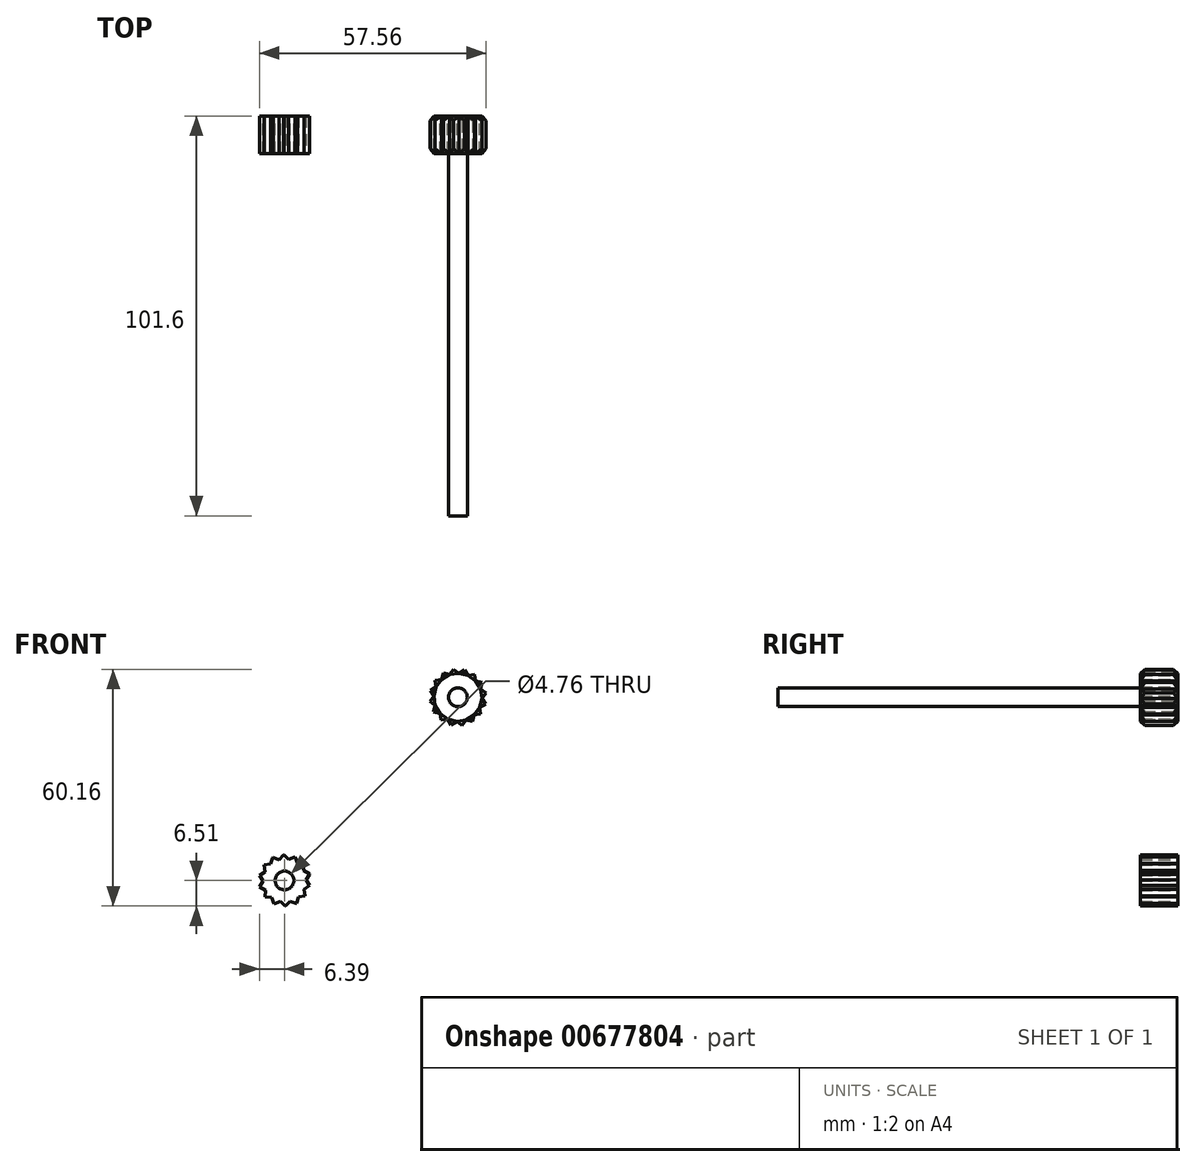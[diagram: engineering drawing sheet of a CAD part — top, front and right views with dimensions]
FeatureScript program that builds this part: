
annotation { "Feature Type Name" : "Feature", "Feature Type Description" : "" }
export const myFeature = defineFeature(function(context is Context, id is Id, definition is map)
    precondition{}
    {
        {
            var Q0;
            Q0=qCreatedBy(makeId("Front.planeOp"),FACE);
            var sketch = newSketch(context, id + "F0", { "sketchPlane" : qUnion([Q0])});
            skCircle(sketch, "E0.cCircle", {"center": v(0, 0) * mm, "radius": 5.32 * mm, "construction": true});
            skLineSegment(sketch, "E0.0", {"start": v(4.98, -2.23) * mm, "end": v(3.52, -4.17) * mm});
            skLineSegment(sketch, "E0.1", {"start": v(3.52, -4.17) * mm, "end": v(1.36, -5.29) * mm});
            skLineSegment(sketch, "E0.2", {"start": v(1.36, -5.29) * mm, "end": v(-1.07, -5.35) * mm});
            skLineSegment(sketch, "E0.3", {"start": v(-1.07, -5.35) * mm, "end": v(-3.28, -4.36) * mm});
            skLineSegment(sketch, "E0.4", {"start": v(-3.28, -4.36) * mm, "end": v(-4.85, -2.5) * mm});
            skLineSegment(sketch, "E0.5", {"start": v(-4.85, -2.5) * mm, "end": v(-5.46, -0.15) * mm});
            skLineSegment(sketch, "E0.6", {"start": v(-5.46, -0.15) * mm, "end": v(-4.98, 2.23) * mm});
            skLineSegment(sketch, "E0.7", {"start": v(-4.98, 2.23) * mm, "end": v(-3.52, 4.17) * mm});
            skLineSegment(sketch, "E0.8", {"start": v(-3.52, 4.17) * mm, "end": v(-1.36, 5.29) * mm});
            skLineSegment(sketch, "E0.9", {"start": v(-1.36, 5.29) * mm, "end": v(1.07, 5.35) * mm});
            skLineSegment(sketch, "E0.10", {"start": v(1.07, 5.35) * mm, "end": v(3.28, 4.36) * mm});
            skLineSegment(sketch, "E0.11", {"start": v(3.28, 4.36) * mm, "end": v(4.85, 2.5) * mm});
            skLineSegment(sketch, "E0.12", {"start": v(4.85, 2.5) * mm, "end": v(5.46, 0.15) * mm});
            skLineSegment(sketch, "E0.13", {"start": v(5.46, 0.15) * mm, "end": v(4.98, -2.23) * mm});
            skPoint(sketch, "E0.0.midPoint", {"position": v(4.25, -3.2) * mm});
            skSolve(sketch);
        }
        {
            var Q0;
            Q0 = qSketchRegion(id + "F0", true);
            extrude(context, id + "F1", {"entities" : qUnion([Q0]), "depth" : 9.52 * mm, "offsetDistance" : 25.4 * mm});
        }
        {
            var Q0;
            Q0=makeQuery(id+"F1.opExtrude","SWEPT_FACE",FACE,{"disambiguationData":[OSD([sQuery(id+"F0.wireOp",EDGE,"E0.12")])]});
            extrude(context, id + "F2", {"entities" : qUnion([Q0]), "operationType" : NewBodyOperationType.ADD, "depth" : 1.2 * mm, "offsetDistance" : 25.4 * mm});
        }
        {
            var Q0;
            Q0=makeQuery(id+"F1.opExtrude","SWEPT_FACE",FACE,{"disambiguationData":[OSD([sQuery(id+"F0.wireOp",EDGE,"E0.13")])]});
            extrude(context, id + "F3", {"entities" : qUnion([Q0]), "operationType" : NewBodyOperationType.ADD, "depth" : 1.2 * mm, "offsetDistance" : 25.4 * mm});
        }
        {
            var Q0;
            Q0=makeQuery(id+"F1.opExtrude","SWEPT_FACE",FACE,{"disambiguationData":[OSD([sQuery(id+"F0.wireOp",EDGE,"E0.0")])]});
            extrude(context, id + "F4", {"entities" : qUnion([Q0]), "operationType" : NewBodyOperationType.ADD, "depth" : 1.2 * mm, "offsetDistance" : 25.4 * mm});
        }
        {
            var Q0;
            Q0=makeQuery(id+"F1.opExtrude","SWEPT_FACE",FACE,{"disambiguationData":[OSD([sQuery(id+"F0.wireOp",EDGE,"E0.11")])]});
            extrude(context, id + "F5", {"entities" : qUnion([Q0]), "operationType" : NewBodyOperationType.ADD, "depth" : 1.2 * mm, "offsetDistance" : 25.4 * mm});
        }
        {
            var Q0;
            Q0=makeQuery(id+"F1.opExtrude","SWEPT_FACE",FACE,{"disambiguationData":[OSD([sQuery(id+"F0.wireOp",EDGE,"E0.10")])]});
            extrude(context, id + "F6", {"entities" : qUnion([Q0]), "operationType" : NewBodyOperationType.ADD, "depth" : 1.2 * mm, "offsetDistance" : 25.4 * mm});
        }
        {
            var Q0;
            Q0=makeQuery(id+"F1.opExtrude","SWEPT_FACE",FACE,{"disambiguationData":[OSD([sQuery(id+"F0.wireOp",EDGE,"E0.9")])]});
            extrude(context, id + "F7", {"entities" : qUnion([Q0]), "operationType" : NewBodyOperationType.ADD, "depth" : 1.2 * mm, "offsetDistance" : 25.4 * mm});
        }
        {
            var Q0;
            Q0=makeQuery(id+"F1.opExtrude","SWEPT_FACE",FACE,{"disambiguationData":[OSD([sQuery(id+"F0.wireOp",EDGE,"E0.8")])]});
            extrude(context, id + "F8", {"entities" : qUnion([Q0]), "operationType" : NewBodyOperationType.ADD, "depth" : 1.2 * mm, "offsetDistance" : 25.4 * mm});
        }
        {
            var Q0;
            Q0=makeQuery(id+"F1.opExtrude","SWEPT_FACE",FACE,{"disambiguationData":[OSD([sQuery(id+"F0.wireOp",EDGE,"E0.7")])]});
            extrude(context, id + "F9", {"entities" : qUnion([Q0]), "operationType" : NewBodyOperationType.ADD, "depth" : 1.2 * mm, "offsetDistance" : 25.4 * mm});
        }
        {
            var Q0;
            Q0=makeQuery(id+"F1.opExtrude","SWEPT_FACE",FACE,{"disambiguationData":[OSD([sQuery(id+"F0.wireOp",EDGE,"E0.6")])]});
            extrude(context, id + "F10", {"entities" : qUnion([Q0]), "operationType" : NewBodyOperationType.ADD, "depth" : 1.2 * mm, "offsetDistance" : 25.4 * mm});
        }
        {
            var Q0;
            Q0=makeQuery(id+"F1.opExtrude","SWEPT_FACE",FACE,{"disambiguationData":[OSD([sQuery(id+"F0.wireOp",EDGE,"E0.5")])]});
            extrude(context, id + "F11", {"entities" : qUnion([Q0]), "operationType" : NewBodyOperationType.ADD, "depth" : 1.2 * mm, "offsetDistance" : 25.4 * mm});
        }
        {
            var Q0;
            Q0=makeQuery(id+"F1.opExtrude","SWEPT_FACE",FACE,{"disambiguationData":[OSD([sQuery(id+"F0.wireOp",EDGE,"E0.4")])]});
            extrude(context, id + "F12", {"entities" : qUnion([Q0]), "operationType" : NewBodyOperationType.ADD, "depth" : 1.2 * mm, "offsetDistance" : 25.4 * mm});
        }
        {
            var Q0;
            Q0=makeQuery(id+"F1.opExtrude","SWEPT_FACE",FACE,{"disambiguationData":[OSD([sQuery(id+"F0.wireOp",EDGE,"E0.3")])]});
            extrude(context, id + "F13", {"entities" : qUnion([Q0]), "operationType" : NewBodyOperationType.ADD, "depth" : 1.2 * mm, "offsetDistance" : 25.4 * mm});
        }
        {
            var Q0;
            Q0=makeQuery(id+"F1.opExtrude","SWEPT_FACE",FACE,{"disambiguationData":[OSD([sQuery(id+"F0.wireOp",EDGE,"E0.2")])]});
            extrude(context, id + "F14", {"entities" : qUnion([Q0]), "operationType" : NewBodyOperationType.ADD, "depth" : 1.2 * mm, "offsetDistance" : 25.4 * mm});
        }
        {
            var Q0;
            Q0=makeQuery(id+"F1.opExtrude","SWEPT_FACE",FACE,{"disambiguationData":[OSD([sQuery(id+"F0.wireOp",EDGE,"E0.1")])]});
            extrude(context, id + "F15", {"entities" : qUnion([Q0]), "operationType" : NewBodyOperationType.ADD, "depth" : 1.2 * mm, "offsetDistance" : 25.4 * mm});
        }
        {
            var Q0;
            Q0=makeQuery(id+"F4.opExtrude","CAP_EDGE",EDGE,{"disambiguationData":[OSD([sQuery(id+"F0.wireOp",EDGE,"E0.0"),sQuery(id+"F0.wireOp",EDGE,"E0.1")])],"isStart":false});
            var Q1;
            Q1=makeQuery(id+"F15.opExtrude","CAP_EDGE",EDGE,{"disambiguationData":[OSD([sQuery(id+"F0.wireOp",EDGE,"E0.0"),sQuery(id+"F0.wireOp",EDGE,"E0.1")])],"isStart":false});
            var Q2;
            Q2=makeQuery(id+"F15.opExtrude","CAP_EDGE",EDGE,{"disambiguationData":[OSD([sQuery(id+"F0.wireOp",EDGE,"E0.1"),sQuery(id+"F0.wireOp",EDGE,"E0.2")])],"isStart":false});
            var Q3;
            Q3=makeQuery(id+"F4.opExtrude","CAP_EDGE",EDGE,{"disambiguationData":[OSD([sQuery(id+"F0.wireOp",EDGE,"E0.0"),sQuery(id+"F0.wireOp",EDGE,"E0.13")])],"isStart":false});
            var Q4;
            Q4=makeQuery(id+"F3.opExtrude","CAP_EDGE",EDGE,{"disambiguationData":[OSD([sQuery(id+"F0.wireOp",EDGE,"E0.0"),sQuery(id+"F0.wireOp",EDGE,"E0.13")])],"isStart":false});
            var Q5;
            Q5=makeQuery(id+"F3.opExtrude","CAP_EDGE",EDGE,{"disambiguationData":[OSD([sQuery(id+"F0.wireOp",EDGE,"E0.12"),sQuery(id+"F0.wireOp",EDGE,"E0.13")])],"isStart":false});
            var Q6;
            Q6=makeQuery(id+"F2.opExtrude","CAP_EDGE",EDGE,{"disambiguationData":[OSD([sQuery(id+"F0.wireOp",EDGE,"E0.12"),sQuery(id+"F0.wireOp",EDGE,"E0.13")])],"isStart":false});
            var Q7;
            Q7=makeQuery(id+"F5.opExtrude","CAP_EDGE",EDGE,{"disambiguationData":[OSD([sQuery(id+"F0.wireOp",EDGE,"E0.11"),sQuery(id+"F0.wireOp",EDGE,"E0.12")])],"isStart":false});
            var Q8;
            Q8=makeQuery(id+"F2.opExtrude","CAP_EDGE",EDGE,{"disambiguationData":[OSD([sQuery(id+"F0.wireOp",EDGE,"E0.11"),sQuery(id+"F0.wireOp",EDGE,"E0.12")])],"isStart":false});
            var Q9;
            Q9=makeQuery(id+"F5.opExtrude","CAP_EDGE",EDGE,{"disambiguationData":[OSD([sQuery(id+"F0.wireOp",EDGE,"E0.10"),sQuery(id+"F0.wireOp",EDGE,"E0.11")])],"isStart":false});
            var Q10;
            Q10=makeQuery(id+"F6.opExtrude","CAP_EDGE",EDGE,{"disambiguationData":[OSD([sQuery(id+"F0.wireOp",EDGE,"E0.10"),sQuery(id+"F0.wireOp",EDGE,"E0.11")])],"isStart":false});
            var Q11;
            Q11=makeQuery(id+"F6.opExtrude","CAP_EDGE",EDGE,{"disambiguationData":[OSD([sQuery(id+"F0.wireOp",EDGE,"E0.9"),sQuery(id+"F0.wireOp",EDGE,"E0.10")])],"isStart":false});
            var Q12;
            Q12=makeQuery(id+"F7.opExtrude","CAP_EDGE",EDGE,{"disambiguationData":[OSD([sQuery(id+"F0.wireOp",EDGE,"E0.9"),sQuery(id+"F0.wireOp",EDGE,"E0.10")])],"isStart":false});
            var Q13;
            Q13=makeQuery(id+"F8.opExtrude","CAP_EDGE",EDGE,{"disambiguationData":[OSD([sQuery(id+"F0.wireOp",EDGE,"E0.8"),sQuery(id+"F0.wireOp",EDGE,"E0.9")])],"isStart":false});
            var Q14;
            Q14=makeQuery(id+"F7.opExtrude","CAP_EDGE",EDGE,{"disambiguationData":[OSD([sQuery(id+"F0.wireOp",EDGE,"E0.8"),sQuery(id+"F0.wireOp",EDGE,"E0.9")])],"isStart":false});
            var Q15;
            Q15=makeQuery(id+"F8.opExtrude","CAP_EDGE",EDGE,{"disambiguationData":[OSD([sQuery(id+"F0.wireOp",EDGE,"E0.7"),sQuery(id+"F0.wireOp",EDGE,"E0.8")])],"isStart":false});
            var Q16;
            Q16=makeQuery(id+"F9.opExtrude","CAP_EDGE",EDGE,{"disambiguationData":[OSD([sQuery(id+"F0.wireOp",EDGE,"E0.7"),sQuery(id+"F0.wireOp",EDGE,"E0.8")])],"isStart":false});
            var Q17;
            Q17=makeQuery(id+"F10.opExtrude","CAP_EDGE",EDGE,{"disambiguationData":[OSD([sQuery(id+"F0.wireOp",EDGE,"E0.6"),sQuery(id+"F0.wireOp",EDGE,"E0.7")])],"isStart":false});
            var Q18;
            Q18=makeQuery(id+"F9.opExtrude","CAP_EDGE",EDGE,{"disambiguationData":[OSD([sQuery(id+"F0.wireOp",EDGE,"E0.6"),sQuery(id+"F0.wireOp",EDGE,"E0.7")])],"isStart":false});
            var Q19;
            Q19=makeQuery(id+"F10.opExtrude","CAP_EDGE",EDGE,{"disambiguationData":[OSD([sQuery(id+"F0.wireOp",EDGE,"E0.5"),sQuery(id+"F0.wireOp",EDGE,"E0.6")])],"isStart":false});
            var Q20;
            Q20=makeQuery(id+"F11.opExtrude","CAP_EDGE",EDGE,{"disambiguationData":[OSD([sQuery(id+"F0.wireOp",EDGE,"E0.5"),sQuery(id+"F0.wireOp",EDGE,"E0.6")])],"isStart":false});
            var Q21;
            Q21=makeQuery(id+"F11.opExtrude","CAP_EDGE",EDGE,{"disambiguationData":[OSD([sQuery(id+"F0.wireOp",EDGE,"E0.4"),sQuery(id+"F0.wireOp",EDGE,"E0.5")])],"isStart":false});
            var Q22;
            Q22=makeQuery(id+"F12.opExtrude","CAP_EDGE",EDGE,{"disambiguationData":[OSD([sQuery(id+"F0.wireOp",EDGE,"E0.4"),sQuery(id+"F0.wireOp",EDGE,"E0.5")])],"isStart":false});
            var Q23;
            Q23=makeQuery(id+"F13.opExtrude","CAP_EDGE",EDGE,{"disambiguationData":[OSD([sQuery(id+"F0.wireOp",EDGE,"E0.3"),sQuery(id+"F0.wireOp",EDGE,"E0.4")])],"isStart":false});
            var Q24;
            Q24=makeQuery(id+"F12.opExtrude","CAP_EDGE",EDGE,{"disambiguationData":[OSD([sQuery(id+"F0.wireOp",EDGE,"E0.3"),sQuery(id+"F0.wireOp",EDGE,"E0.4")])],"isStart":false});
            var Q25;
            Q25=makeQuery(id+"F13.opExtrude","CAP_EDGE",EDGE,{"disambiguationData":[OSD([sQuery(id+"F0.wireOp",EDGE,"E0.2"),sQuery(id+"F0.wireOp",EDGE,"E0.3")])],"isStart":false});
            var Q26;
            Q26=makeQuery(id+"F14.opExtrude","CAP_EDGE",EDGE,{"disambiguationData":[OSD([sQuery(id+"F0.wireOp",EDGE,"E0.2"),sQuery(id+"F0.wireOp",EDGE,"E0.3")])],"isStart":false});
            var Q27;
            Q27=makeQuery(id+"F14.opExtrude","CAP_EDGE",EDGE,{"disambiguationData":[OSD([sQuery(id+"F0.wireOp",EDGE,"E0.1"),sQuery(id+"F0.wireOp",EDGE,"E0.2")])],"isStart":false});
            chamfer(context, id + "F16", {"entities" : qUnion([Q0, Q1, Q2, Q3, Q4, Q5, Q6, Q7, Q8, Q9, Q10, Q11, Q12, Q13, Q14, Q15, Q16, Q17, Q18, Q19, Q20, Q21, Q22, Q23, Q24, Q25, Q26, Q27]), "width" : 1.2 * mm, "tangentPropagation" : true});
        }
        {
            var Q0;
            Q0=sQuery(id+"F0.wireOp",VERTEX,"E0.cCircle.center");
            var Q1;
            Q1=makeQuery(id+"F1.opExtrude","SWEPT_BODY",BODY,{"disambiguationData":[OSD([sQuery(id+"F0.wireOp",EDGE,"E0.0"),sQuery(id+"F0.wireOp",EDGE,"E0.1"),sQuery(id+"F0.wireOp",EDGE,"E0.2"),sQuery(id+"F0.wireOp",EDGE,"E0.3"),sQuery(id+"F0.wireOp",EDGE,"E0.4"),sQuery(id+"F0.wireOp",EDGE,"E0.5"),sQuery(id+"F0.wireOp",EDGE,"E0.6"),sQuery(id+"F0.wireOp",EDGE,"E0.7"),sQuery(id+"F0.wireOp",EDGE,"E0.8"),sQuery(id+"F0.wireOp",EDGE,"E0.9"),sQuery(id+"F0.wireOp",EDGE,"E0.10"),sQuery(id+"F0.wireOp",EDGE,"E0.11"),sQuery(id+"F0.wireOp",EDGE,"E0.12"),sQuery(id+"F0.wireOp",EDGE,"E0.13")])]});
            hole(context, id + "F17", {"style" : HoleStyle.SIMPLE, "endStyle" : HoleEndStyle.THROUGH, "oppositeDirection" : true, "holeDiameter" : 4.76 * mm, "majorDiameter" : 6.35 * mm, "isTappedThrough" : true, "tappedDepth" : 12.7 * mm, "tapClearance" : 3, "locations" : qUnion([Q0]), "scope" : qUnion([Q1])});
        }
        {
            var Q0;
            Q0=qCreatedBy(makeId("Front.planeOp"),FACE);
            var sketch = newSketch(context, id + "F18", { "sketchPlane" : qUnion([Q0])});
            skCircle(sketch, "E1.cCircle", {"center": v(44.05, 46.54) * mm, "radius": 6 * mm, "construction": true});
            skLineSegment(sketch, "E1.0", {"start": v(50.16, 46.25) * mm, "end": v(49.59, 43.93) * mm});
            skLineSegment(sketch, "E1.1", {"start": v(49.59, 43.93) * mm, "end": v(48.17, 42) * mm});
            skLineSegment(sketch, "E1.2", {"start": v(48.17, 42) * mm, "end": v(46.12, 40.78) * mm});
            skLineSegment(sketch, "E1.3", {"start": v(46.12, 40.78) * mm, "end": v(43.76, 40.42) * mm});
            skLineSegment(sketch, "E1.4", {"start": v(43.76, 40.42) * mm, "end": v(41.45, 41) * mm});
            skLineSegment(sketch, "E1.5", {"start": v(41.45, 41) * mm, "end": v(39.52, 42.42) * mm});
            skLineSegment(sketch, "E1.6", {"start": v(39.52, 42.42) * mm, "end": v(38.3, 44.46) * mm});
            skLineSegment(sketch, "E1.7", {"start": v(38.3, 44.46) * mm, "end": v(37.94, 46.82) * mm});
            skLineSegment(sketch, "E1.8", {"start": v(37.94, 46.82) * mm, "end": v(38.51, 49.14) * mm});
            skLineSegment(sketch, "E1.9", {"start": v(38.51, 49.14) * mm, "end": v(39.93, 51.06) * mm});
            skLineSegment(sketch, "E1.10", {"start": v(39.93, 51.06) * mm, "end": v(41.98, 52.3) * mm});
            skLineSegment(sketch, "E1.11", {"start": v(41.98, 52.3) * mm, "end": v(44.34, 52.65) * mm});
            skLineSegment(sketch, "E1.12", {"start": v(44.34, 52.65) * mm, "end": v(46.66, 52.07) * mm});
            skLineSegment(sketch, "E1.13", {"start": v(46.66, 52.07) * mm, "end": v(48.58, 50.65) * mm});
            skLineSegment(sketch, "E1.14", {"start": v(48.58, 50.65) * mm, "end": v(49.8, 48.6) * mm});
            skLineSegment(sketch, "E1.15", {"start": v(49.8, 48.6) * mm, "end": v(50.16, 46.25) * mm});
            skPoint(sketch, "E1.0.midPoint", {"position": v(49.88, 45.09) * mm});
            skCircle(sketch, "E2", {"center": v(44.05, 46.54) * mm, "radius": 2.38 * mm});
            skSolve(sketch);
        }
        {
            var Q0;
            Q0=makeQuery(id+"F18.imprint","IMPRINT",FACE,{"disambiguationData":[TD([[makeQuery(id+"F18.imprint","IMPRINT",EDGE,{"derivedFrom":sQuery(id+"F18.wireOp",EDGE,"E1.0")}),-1.0]])]});
            extrude(context, id + "F19", {"entities" : qUnion([Q0]), "depth" : 9.52 * mm, "offsetDistance" : 25.4 * mm});
        }
        {
            var Q0;
            Q0=makeQuery(id+"F19.opExtrude","SWEPT_FACE",FACE,{"disambiguationData":[OSD([sQuery(id+"F18.wireOp",EDGE,"E1.2")])]});
            extrude(context, id + "F20", {"entities" : qUnion([Q0]), "operationType" : NewBodyOperationType.ADD, "depth" : 1.2 * mm, "offsetDistance" : 25.4 * mm});
        }
        {
            var Q0;
            Q0=makeQuery(id+"F19.opExtrude","SWEPT_FACE",FACE,{"disambiguationData":[OSD([sQuery(id+"F18.wireOp",EDGE,"E1.4")])]});
            extrude(context, id + "F21", {"entities" : qUnion([Q0]), "operationType" : NewBodyOperationType.ADD, "depth" : 1.2 * mm, "offsetDistance" : 25.4 * mm});
        }
        {
            var Q0;
            Q0=makeQuery(id+"F19.opExtrude","SWEPT_FACE",FACE,{"disambiguationData":[OSD([sQuery(id+"F18.wireOp",EDGE,"E1.6")])]});
            extrude(context, id + "F22", {"entities" : qUnion([Q0]), "operationType" : NewBodyOperationType.ADD, "depth" : 1.2 * mm, "offsetDistance" : 25.4 * mm});
        }
        {
            var Q0;
            Q0=makeQuery(id+"F19.opExtrude","SWEPT_FACE",FACE,{"disambiguationData":[OSD([sQuery(id+"F18.wireOp",EDGE,"E1.8")])]});
            extrude(context, id + "F23", {"entities" : qUnion([Q0]), "operationType" : NewBodyOperationType.ADD, "depth" : 1.2 * mm, "offsetDistance" : 25.4 * mm});
        }
        {
            var Q0;
            Q0=makeQuery(id+"F19.opExtrude","SWEPT_FACE",FACE,{"disambiguationData":[OSD([sQuery(id+"F18.wireOp",EDGE,"E1.10")])]});
            extrude(context, id + "F24", {"entities" : qUnion([Q0]), "operationType" : NewBodyOperationType.ADD, "depth" : 1.2 * mm, "offsetDistance" : 25.4 * mm});
        }
        {
            var Q0;
            Q0=makeQuery(id+"F19.opExtrude","SWEPT_FACE",FACE,{"disambiguationData":[OSD([sQuery(id+"F18.wireOp",EDGE,"E1.12")])]});
            extrude(context, id + "F25", {"entities" : qUnion([Q0]), "operationType" : NewBodyOperationType.ADD, "depth" : 1.2 * mm, "offsetDistance" : 25.4 * mm});
        }
        {
            var Q0;
            Q0=makeQuery(id+"F19.opExtrude","SWEPT_FACE",FACE,{"disambiguationData":[OSD([sQuery(id+"F18.wireOp",EDGE,"E1.14")])]});
            extrude(context, id + "F26", {"entities" : qUnion([Q0]), "operationType" : NewBodyOperationType.ADD, "depth" : 1.2 * mm, "offsetDistance" : 25.4 * mm});
        }
        {
            var Q0;
            Q0=makeQuery(id+"F19.opExtrude","SWEPT_FACE",FACE,{"disambiguationData":[OSD([sQuery(id+"F18.wireOp",EDGE,"E1.0")])]});
            extrude(context, id + "F27", {"entities" : qUnion([Q0]), "operationType" : NewBodyOperationType.ADD, "depth" : 1.2 * mm, "offsetDistance" : 25.4 * mm});
        }
        {
            var Q0;
            Q0=makeQuery(id+"F26.opExtrude","CAP_FACE",FACE,{"disambiguationData":[OSD([sQuery(id+"F18.wireOp",EDGE,"E1.14")])],"isStart":false});
            var Q1;
            Q1=makeQuery(id+"F25.opExtrude","CAP_FACE",FACE,{"disambiguationData":[OSD([sQuery(id+"F18.wireOp",EDGE,"E1.12")])],"isStart":false});
            var Q2;
            Q2=makeQuery(id+"F27.opExtrude","CAP_FACE",FACE,{"disambiguationData":[OSD([sQuery(id+"F18.wireOp",EDGE,"E1.0")])],"isStart":false});
            var Q3;
            Q3=makeQuery(id+"F20.opExtrude","CAP_FACE",FACE,{"disambiguationData":[OSD([sQuery(id+"F18.wireOp",EDGE,"E1.2")])],"isStart":false});
            var Q4;
            Q4=makeQuery(id+"F21.opExtrude","CAP_FACE",FACE,{"disambiguationData":[OSD([sQuery(id+"F18.wireOp",EDGE,"E1.4")])],"isStart":false});
            var Q5;
            Q5=makeQuery(id+"F22.opExtrude","CAP_FACE",FACE,{"disambiguationData":[OSD([sQuery(id+"F18.wireOp",EDGE,"E1.6")])],"isStart":false});
            var Q6;
            Q6=makeQuery(id+"F23.opExtrude","CAP_FACE",FACE,{"disambiguationData":[OSD([sQuery(id+"F18.wireOp",EDGE,"E1.8")])],"isStart":false});
            var Q7;
            Q7=makeQuery(id+"F24.opExtrude","CAP_FACE",FACE,{"disambiguationData":[OSD([sQuery(id+"F18.wireOp",EDGE,"E1.10")])],"isStart":false});
            chamfer(context, id + "F28", {"entities" : qUnion([Q0, Q1, Q2, Q3, Q4, Q5, Q6, Q7]), "width" : 1.2 * mm, "tangentPropagation" : true});
        }
        {
            var Q0;
            Q0=makeQuery(id+"F19.opExtrude","SWEPT_FACE",FACE,{"disambiguationData":[OSD([sQuery(id+"F18.wireOp",EDGE,"E1.9")])]});
            extrude(context, id + "F29", {"entities" : qUnion([Q0]), "operationType" : NewBodyOperationType.ADD, "depth" : 1.2 * mm, "offsetDistance" : 25.4 * mm});
        }
        {
            var Q0;
            Q0=makeQuery(id+"F19.opExtrude","SWEPT_FACE",FACE,{"disambiguationData":[OSD([sQuery(id+"F18.wireOp",EDGE,"E1.11")])]});
            extrude(context, id + "F30", {"entities" : qUnion([Q0]), "operationType" : NewBodyOperationType.ADD, "depth" : 1.2 * mm, "offsetDistance" : 25.4 * mm});
        }
        {
            var Q0;
            Q0=makeQuery(id+"F19.opExtrude","SWEPT_FACE",FACE,{"disambiguationData":[OSD([sQuery(id+"F18.wireOp",EDGE,"E1.13")])]});
            extrude(context, id + "F31", {"entities" : qUnion([Q0]), "operationType" : NewBodyOperationType.ADD, "depth" : 1.2 * mm, "offsetDistance" : 25.4 * mm});
        }
        {
            var Q0;
            Q0=makeQuery(id+"F19.opExtrude","SWEPT_FACE",FACE,{"disambiguationData":[OSD([sQuery(id+"F18.wireOp",EDGE,"E1.15")])]});
            extrude(context, id + "F32", {"entities" : qUnion([Q0]), "operationType" : NewBodyOperationType.ADD, "depth" : 1.2 * mm, "offsetDistance" : 25.4 * mm});
        }
        {
            var Q0;
            Q0=makeQuery(id+"F19.opExtrude","SWEPT_FACE",FACE,{"disambiguationData":[OSD([sQuery(id+"F18.wireOp",EDGE,"E1.1")])]});
            extrude(context, id + "F33", {"entities" : qUnion([Q0]), "operationType" : NewBodyOperationType.ADD, "depth" : 1.2 * mm, "offsetDistance" : 25.4 * mm});
        }
        {
            var Q0;
            Q0=makeQuery(id+"F19.opExtrude","SWEPT_FACE",FACE,{"disambiguationData":[OSD([sQuery(id+"F18.wireOp",EDGE,"E1.3")])]});
            extrude(context, id + "F34", {"entities" : qUnion([Q0]), "operationType" : NewBodyOperationType.ADD, "depth" : 1.2 * mm, "offsetDistance" : 25.4 * mm});
        }
        {
            var Q0;
            Q0=makeQuery(id+"F19.opExtrude","SWEPT_FACE",FACE,{"disambiguationData":[OSD([sQuery(id+"F18.wireOp",EDGE,"E1.5")])]});
            extrude(context, id + "F35", {"entities" : qUnion([Q0]), "operationType" : NewBodyOperationType.ADD, "depth" : 1.2 * mm, "offsetDistance" : 25.4 * mm});
        }
        {
            var Q0;
            Q0=makeQuery(id+"F19.opExtrude","SWEPT_FACE",FACE,{"disambiguationData":[OSD([sQuery(id+"F18.wireOp",EDGE,"E1.7")])]});
            extrude(context, id + "F36", {"entities" : qUnion([Q0]), "operationType" : NewBodyOperationType.ADD, "depth" : 1.2 * mm, "offsetDistance" : 25.4 * mm});
        }
        {
            var Q0;
            Q0=makeQuery(id+"F36.opExtrude","CAP_FACE",FACE,{"disambiguationData":[OSD([sQuery(id+"F18.wireOp",EDGE,"E1.7")])],"isStart":false});
            var Q1;
            Q1=makeQuery(id+"F29.opExtrude","CAP_FACE",FACE,{"disambiguationData":[OSD([sQuery(id+"F18.wireOp",EDGE,"E1.9")])],"isStart":false});
            var Q2;
            Q2=makeQuery(id+"F35.opExtrude","CAP_FACE",FACE,{"disambiguationData":[OSD([sQuery(id+"F18.wireOp",EDGE,"E1.5")])],"isStart":false});
            var Q3;
            Q3=makeQuery(id+"F34.opExtrude","CAP_FACE",FACE,{"disambiguationData":[OSD([sQuery(id+"F18.wireOp",EDGE,"E1.3")])],"isStart":false});
            var Q4;
            Q4=makeQuery(id+"F30.opExtrude","CAP_FACE",FACE,{"disambiguationData":[OSD([sQuery(id+"F18.wireOp",EDGE,"E1.11")])],"isStart":false});
            var Q5;
            Q5=makeQuery(id+"F31.opExtrude","CAP_FACE",FACE,{"disambiguationData":[OSD([sQuery(id+"F18.wireOp",EDGE,"E1.13")])],"isStart":false});
            var Q6;
            Q6=makeQuery(id+"F32.opExtrude","CAP_FACE",FACE,{"disambiguationData":[OSD([sQuery(id+"F18.wireOp",EDGE,"E1.15")])],"isStart":false});
            var Q7;
            Q7=makeQuery(id+"F33.opExtrude","CAP_FACE",FACE,{"disambiguationData":[OSD([sQuery(id+"F18.wireOp",EDGE,"E1.1")])],"isStart":false});
            chamfer(context, id + "F37", {"entities" : qUnion([Q0, Q1, Q2, Q3, Q4, Q5, Q6, Q7]), "width" : 1.2 * mm, "tangentPropagation" : true});
        }
        {
            var Q0;
            Q0=makeQuery(id+"F18.imprint","IMPRINT",FACE,{"disambiguationData":[TD([[makeQuery(id+"F18.imprint","IMPRINT",EDGE,{"derivedFrom":sQuery(id+"F18.wireOp",EDGE,"E2")}),1.0]])]});
            extrude(context, id + "F38", {"entities" : qUnion([Q0]), "operationType" : NewBodyOperationType.ADD, "depth" : 101.6 * mm, "offsetDistance" : 25.4 * mm});
        }
    });
